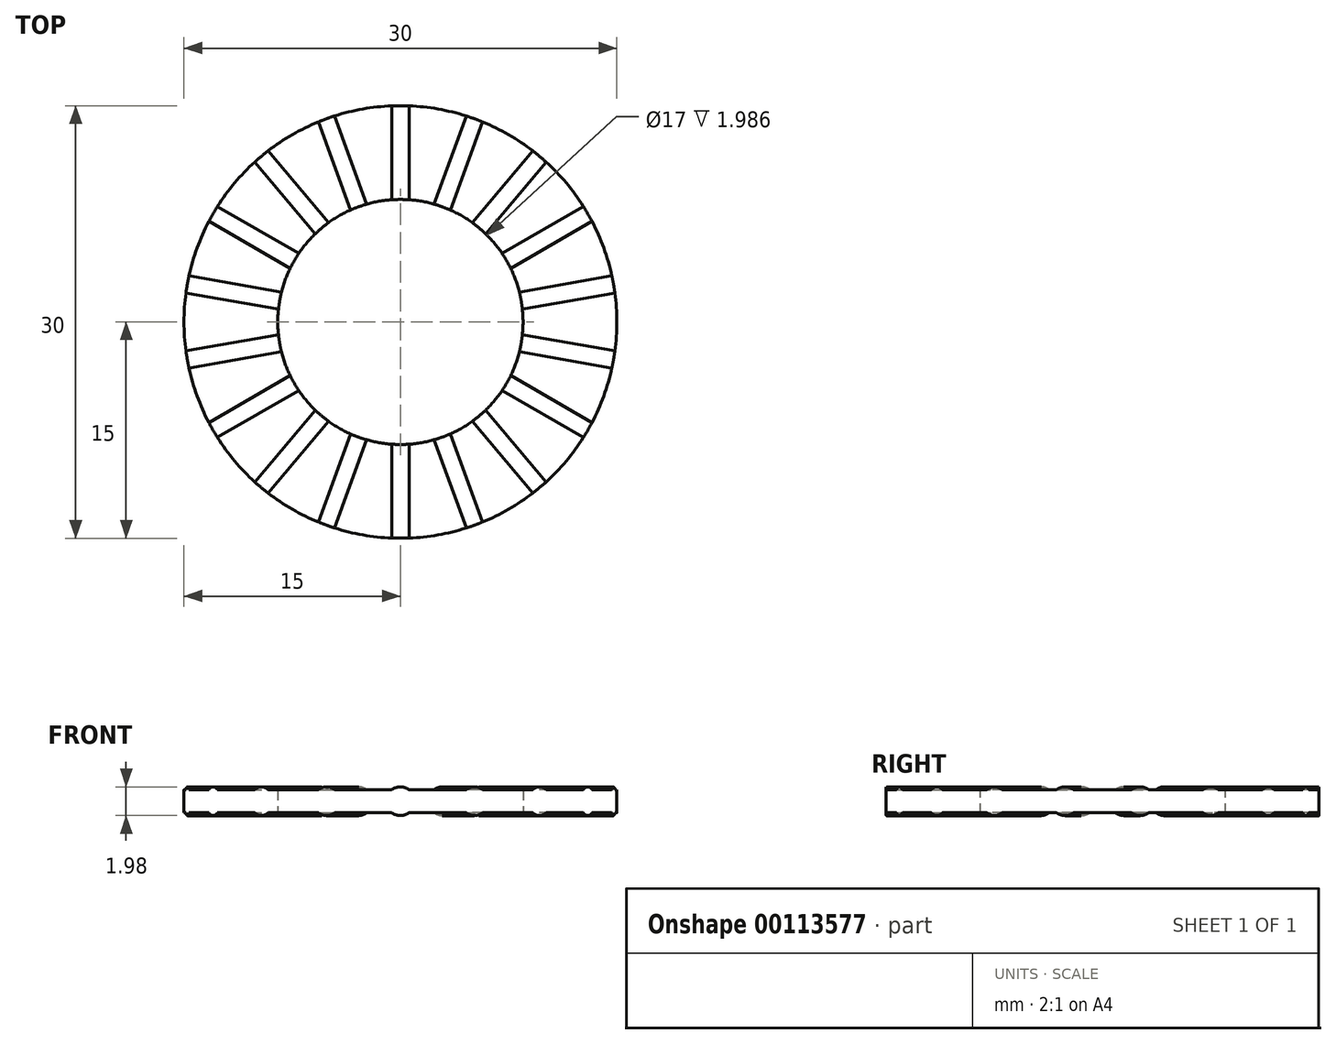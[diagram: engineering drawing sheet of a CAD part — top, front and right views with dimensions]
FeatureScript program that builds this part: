
annotation { "Feature Type Name" : "Feature", "Feature Type Description" : "" }
export const myFeature = defineFeature(function(context is Context, id is Id, definition is map)
    precondition{}
    {
        {
            var Q0;
            Q0=qCreatedBy(makeId("Top.planeOp"),FACE);
            var sketch = newSketch(context, id + "F0", { "sketchPlane" : qUnion([Q0])});
            skCircle(sketch, "E0", {"center": v(0, 0) * mm, "radius": 8.5 * mm});
            skCircle(sketch, "E1", {"center": v(0, 0) * mm, "radius": 15 * mm});
            skSolve(sketch);
        }
        {
            var Q0;
            Q0 = qSketchRegion(id + "F0", true);
            extrude(context, id + "F1", {"entities" : qUnion([Q0]), "depth" : 0.8 * mm, "hasSecondDirection" : true, "secondDirectionOppositeDirection" : true, "secondDirectionDepth" : 0.8 * mm});
        }
        {
            var Q0;
            Q0=makeQuery(id+"F1.opExtrude","CAP_FACE",FACE,{"disambiguationData":[OSD([sQuery(id+"F0.wireOp",EDGE,"E0"),sQuery(id+"F0.wireOp",EDGE,"E1")])],"isStart":false});
            var sketch = newSketch(context, id + "F2", { "sketchPlane" : qUnion([Q0])});
            skCircle(sketch, "E2", {"center": v(0, 0) * mm, "radius": 9.6 * mm});
            skCircle(sketch, "E3", {"center": v(0, 0) * mm, "radius": 14.25 * mm});
            skSolve(sketch);
        }
        {
            var Q0;
            Q0=qCreatedBy(makeId("Front.planeOp"),FACE);
            var sketch = newSketch(context, id + "F3", { "sketchPlane" : qUnion([Q0])});
            skCircle(sketch, "E4", {"center": v(0, 0) * mm, "radius": 1 * mm});
            skSolve(sketch);
        }
        {
            var Q0;
            Q0 = qSketchRegion(id + "F3", true);
            extrude(context, id + "F4", {"entities" : qUnion([Q0]), "operationType" : NewBodyOperationType.ADD, "depth" : 25 * mm});
        }
        {
            var Q0;
            Q0=makeQuery(id+"F1.opExtrude","SWEPT_BODY",BODY,{"disambiguationData":[OSD([sQuery(id+"F0.wireOp",EDGE,"E0"),sQuery(id+"F0.wireOp",EDGE,"E1")])]});
            var Q1;
            Q1=sQuery(id+"F2.wireOp",EDGE,"E2");
            circularPattern(context, id + "F5", {"operationType" : NewBodyOperationType.ADD, "entities" : qUnion([Q0]), "axis" : qUnion([Q1]), "angle" : 20 * degree, "instanceCount" : 18});
        }
        {
            var Q0;
            Q0=qCreatedBy(makeId("Top.planeOp"),FACE);
            var sketch = newSketch(context, id + "F6", { "sketchPlane" : qUnion([Q0])});
            skCircle(sketch, "E5", {"center": v(0, 0) * mm, "radius": 8.5 * mm});
            skCircle(sketch, "E6", {"center": v(0, 0) * mm, "radius": 15 * mm});
            skCircle(sketch, "E7", {"center": v(0, 0) * mm, "radius": 26 * mm});
            skSolve(sketch);
        }
        {
            var Q0;
            Q0=makeQuery(id+"F6.imprint","IMPRINT",FACE,{"disambiguationData":[TD([[makeQuery(id+"F6.imprint","IMPRINT",EDGE,{"derivedFrom":sQuery(id+"F6.wireOp",EDGE,"E6")}),-1.0]])]});
            var Q1;
            Q1=makeQuery(id+"F6.imprint","IMPRINT",FACE,{"disambiguationData":[TD([[makeQuery(id+"F6.imprint","IMPRINT",EDGE,{"derivedFrom":sQuery(id+"F6.wireOp",EDGE,"E5")}),1.0]])]});
            extrude(context, id + "F7", {"entities" : qUnion([Q0, Q1]), "operationType" : NewBodyOperationType.REMOVE, "endBound" : BoundingType.THROUGH_ALL, "oppositeDirection" : true, "depth" : 25 * mm, "hasSecondDirection" : true, "secondDirectionBound" : SecondDirectionBoundingType.THROUGH_ALL, "secondDirectionOppositeDirection" : false, "secondDirectionDepth" : 25 * mm});
        }
    });
